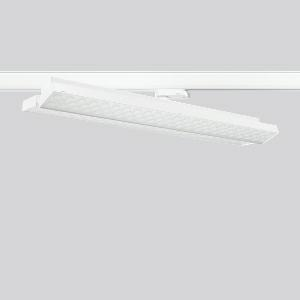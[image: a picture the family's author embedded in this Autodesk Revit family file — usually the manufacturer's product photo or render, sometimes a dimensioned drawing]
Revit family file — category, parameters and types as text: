
# Revit family: tx-move_742162_002_2_1af7
name_source: partatom
category: Lighting Fixtures
units: mm (PartAtom-declared; Revit-internal decimal feet)

## family parameters
Cut with Voids When Loaded = No
Host = Face
Light Source = No
Part Type = Normal
Room Calculation Point = No
Round Connector Dimension = Use Diameter
Shared = No

## types (1)
- MultiLumen 1 (1 x LED Modul 927, 2150 lm, 2700)
    Apparent Load = 38 VA
    CIE Flux Codes = 77 96 99 100 100
    Color Rendering = 92
    Color Temperature = 2700
    Default Elevation = 1800 mm
    Description = Series: TX-MOVE
Multifunctional surface-mounted spotlight for area lighting. Very flat design. Housing: sheet steel, powder-coated. Rotation range: 356°. Swivel range: 90°. Consistent alignment possible with visible tilt scale. High-efficiency LED units with optimum light control thanks to clear plastic (PC) lens optics. Spezielle Mikrostrukturen reduzieren Gelbsaum. Symmetrical light distribution. Best colour rendering with CRI >90 for fresh products and coloured textiles. With multi adaptor for 3-circuit tracks 230 V. Suitable for Track on ceiling. MultiLumen: Luminous flux adjustable in 3 steps. Factory setting is the highest luminous flux. Environmentally friendly and resource-saving due to replaceable and recyclable components. 
Colour: traffic white, matt (RAL 9016)
Length: 570 mm
Width: 119 mm
Height: 92 mm
Lamp: LED
Socket: without socket
Colour temperature: 2700K
Colour rendering index (CRI): 90
System power: 38 W
Rated luminous flux: 4300 lm
Luminous efficiency: 113 lm/W
System power 2: 51 W
Rated luminous flux 2: 5600 lm
Luminous efficiency 2: 110 lm/W
System power 3: 62 W
Rated luminous flux 3: 6650 lm
Luminous efficiency 3: 107 lm/W
Control gear: Regulated power supply
Protection class: I
Type of protection: IP 20
    Height = 75 mm
    Lamp = 1 x LED Modul 927
    Lamp Light Flux = 2150 lm
    Lamp count = 1
    Length = 569 mm
    Lifetime = 50000 h
    Luminous efficacy = 113 lm/W
    Manufacturer = RZB
    ModVariant = No
    Model = 742162.002.2
    Mounting Place = Ceiling
    Mounting Type = Surface mounted
    Number of Poles = 1
    OnlyDefault = Yes
    Power Factor = 1
    Product Name = TX-MOVE
    Product group = Track mounted projectors
    ProductGroupID = 301
    Protection Class = Protection class I
    Protection Degree = IP 20
    RLX_Detail_Level = 1
    RLX_Emergency_Light_Flux = 0 lm
    RLX_Emergency_Type = 0
    RLX_Emergency_Type_DB = No
    RlxData = <blob elided: 31261 chars, md5=a8ca277a>
    Socket = socket
    Standby Power = 0 W
    System Light Flux = 4300 lm
    System Power = 38 W
    Type Comments = MultiLumen 1
    Type Image = 742162.002.jpg
    URL = http://relux.com
    VarID = multilumen_1
    Voltage = 0 V
    Weight = 0.00 kg
    Width = 119 mm

## geometry (parser evidence)
native form markers: Blend x4, Sweep x16
no freeform markers — native parametric forms only
